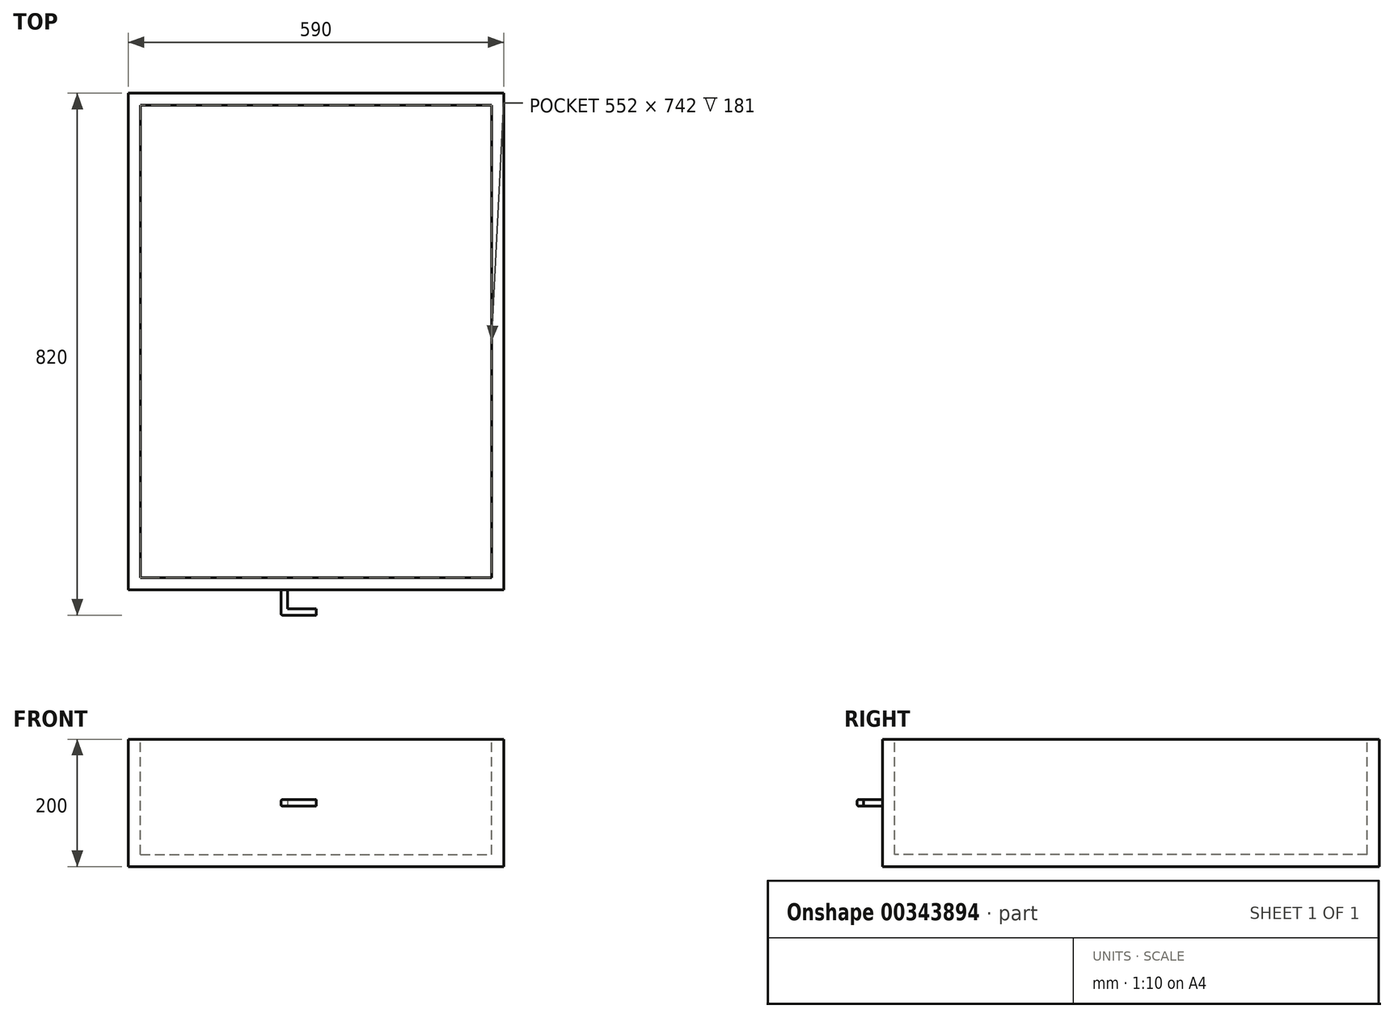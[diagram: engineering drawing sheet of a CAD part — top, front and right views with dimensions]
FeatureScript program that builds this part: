
annotation { "Feature Type Name" : "Feature", "Feature Type Description" : "" }
export const myFeature = defineFeature(function(context is Context, id is Id, definition is map)
    precondition{}
    {
        {
            var Q0;
            Q0=qCreatedBy(makeId("Front.planeOp"),FACE);
            var sketch = newSketch(context, id + "F0", { "sketchPlane" : qUnion([Q0])});
            skLineSegment(sketch, "E0.bottom", {"start": v(-295, 100) * mm, "end": v(295, 100) * mm});
            skLineSegment(sketch, "E0.top", {"start": v(-295, -100) * mm, "end": v(295, -100) * mm});
            skLineSegment(sketch, "E0.left", {"start": v(-295, 100) * mm, "end": v(-295, -100) * mm});
            skLineSegment(sketch, "E0.right", {"start": v(295, 100) * mm, "end": v(295, -100) * mm});
            skPoint(sketch, "E0.middle", {"position": v(0, 0) * mm});
            skSolve(sketch);
        }
        {
            var Q0;
            Q0 = qSketchRegion(id + "F0", true);
            extrude(context, id + "F1", {"entities" : qUnion([Q0]), "depth" : 780 * mm});
        }
        {
            var Q0;
            Q0=makeQuery(id+"F1.opExtrude","SWEPT_FACE",FACE,{"disambiguationData":[OSD([sQuery(id+"F0.wireOp",EDGE,"E0.bottom")])]});
            var sketch = newSketch(context, id + "F2", { "sketchPlane" : qUnion([Q0])});
            skLineSegment(sketch, "E1.bottom", {"start": v(-276, -19) * mm, "end": v(276, -19) * mm});
            skLineSegment(sketch, "E1.top", {"start": v(-276, -761) * mm, "end": v(276, -761) * mm});
            skLineSegment(sketch, "E1.left", {"start": v(-276, -19) * mm, "end": v(-276, -761) * mm});
            skLineSegment(sketch, "E1.right", {"start": v(276, -19) * mm, "end": v(276, -761) * mm});
            skSolve(sketch);
        }
        {
            var Q0;
            Q0=makeQuery(id+"F2.imprint","IMPRINT",FACE,{"disambiguationData":[TD([[makeQuery(id+"F2.imprint","IMPRINT",EDGE,{"derivedFrom":sQuery(id+"F2.wireOp",EDGE,"E1.bottom")}),-1.0]])]});
            extrude(context, id + "F3", {"entities" : qUnion([Q0]), "operationType" : NewBodyOperationType.REMOVE, "oppositeDirection" : true, "depth" : 181 * mm});
        }
        {
            var Q0;
            Q0=makeQuery(id+"F1.opExtrude","CAP_FACE",FACE,{"disambiguationData":[OSD([sQuery(id+"F0.wireOp",EDGE,"E0.bottom"),sQuery(id+"F0.wireOp",EDGE,"E0.top"),sQuery(id+"F0.wireOp",EDGE,"E0.left"),sQuery(id+"F0.wireOp",EDGE,"E0.right")])],"isStart":false});
            var sketch = newSketch(context, id + "F4", { "sketchPlane" : qUnion([Q0])});
            skLineSegment(sketch, "E2.bottom", {"start": v(-45, 5) * mm, "end": v(-55, 5) * mm});
            skLineSegment(sketch, "E2.top", {"start": v(-45, -5) * mm, "end": v(-55, -5) * mm});
            skLineSegment(sketch, "E2.left", {"start": v(-45, 5) * mm, "end": v(-45, -5) * mm});
            skLineSegment(sketch, "E2.right", {"start": v(-55, 5) * mm, "end": v(-55, -5) * mm});
            skPoint(sketch, "E2.middle", {"position": v(-50, 0) * mm});
            skLineSegment(sketch, "E3", {"start": v(-50, 0) * mm, "end": v(0, 0) * mm, "construction": true});
            skSolve(sketch);
        }
        {
            var Q0;
            Q0 = qSketchRegion(id + "F4", true);
            extrude(context, id + "F5", {"entities" : qUnion([Q0]), "operationType" : NewBodyOperationType.ADD, "depth" : 40 * mm});
        }
        {
            var Q0;
            Q0=makeQuery(id+"F5.opExtrude","SWEPT_FACE",FACE,{"disambiguationData":[OSD([sQuery(id+"F4.wireOp",EDGE,"E2.left")])]});
            var sketch = newSketch(context, id + "F6", { "sketchPlane" : qUnion([Q0])});
            skLineSegment(sketch, "E4.bottom", {"start": v(-820, 5) * mm, "end": v(-810, 5) * mm});
            skLineSegment(sketch, "E4.top", {"start": v(-820, -5) * mm, "end": v(-810, -5) * mm});
            skLineSegment(sketch, "E4.left", {"start": v(-820, 5) * mm, "end": v(-820, -5) * mm});
            skLineSegment(sketch, "E4.right", {"start": v(-810, 5) * mm, "end": v(-810, -5) * mm});
            skSolve(sketch);
        }
        {
            var Q0;
            Q0 = qSketchRegion(id + "F6", true);
            var Q1;
            Q1=qCreatedBy(makeId("Right.planeOp"),FACE);
            extrude(context, id + "F7", {"entities" : qUnion([Q0]), "operationType" : NewBodyOperationType.ADD, "endBound" : BoundingType.UP_TO_SURFACE, "endBoundEntityFace" : qUnion([Q1]), "depth" : 25 * mm});
        }
        {
            var Q0;
            {var subQ0=sQuery(id+"F6.wireOp",EDGE,"E4.left");var subQ1=sQuery(id+"F6.wireOp",EDGE,"E4.bottom");var subQ2=sQuery(id+"F4.wireOp",EDGE,"E2.bottom");Q0=makeQuery(id+"FwasGqPcXIY0o4f_1.1.F7.boolean.opBoolean","MERGE",EDGE,{"derivedFrom":[makeQuery(id+"F7.boolean.opBoolean","MERGE",EDGE,{"derivedFrom":[makeQuery(id+"F5.opExtrude","CAP_EDGE",EDGE,{"disambiguationData":[OSD([subQ2])],"isStart":false}),makeQuery(id+"F7.opExtrude","SWEPT_EDGE",EDGE,{"disambiguationData":[OSD([subQ1,subQ0])]})]}),makeQuery(id+"FwasGqPcXIY0o4f_1.1.F5.opExtrude","CAP_EDGE",EDGE,{"disambiguationData":[OSD([subQ2])],"isStart":false}),makeQuery(id+"FwasGqPcXIY0o4f_1.1.F7.opExtrude","SWEPT_EDGE",EDGE,{"disambiguationData":[OSD([subQ1,subQ0])]})]});}
            fillet(context, id + "F8", {"entities" : qUnion([Q0]), "radius" : 2 * mm, "tangentPropagation" : true, "allowEdgeOverflow" : false});
        }
        {
            var Q0;
            {var subQ0=sQuery(id+"F6.wireOp",EDGE,"E4.left");var subQ1=sQuery(id+"F6.wireOp",EDGE,"E4.top");var subQ2=sQuery(id+"F4.wireOp",EDGE,"E2.top");Q0=makeQuery(id+"FwasGqPcXIY0o4f_1.1.F7.boolean.opBoolean","MERGE",EDGE,{"derivedFrom":[makeQuery(id+"F7.boolean.opBoolean","MERGE",EDGE,{"derivedFrom":[makeQuery(id+"F5.opExtrude","CAP_EDGE",EDGE,{"disambiguationData":[OSD([subQ2])],"isStart":false}),makeQuery(id+"F7.opExtrude","SWEPT_EDGE",EDGE,{"disambiguationData":[OSD([subQ1,subQ0])]})]}),makeQuery(id+"FwasGqPcXIY0o4f_1.1.F5.opExtrude","CAP_EDGE",EDGE,{"disambiguationData":[OSD([subQ2])],"isStart":false}),makeQuery(id+"FwasGqPcXIY0o4f_1.1.F7.opExtrude","SWEPT_EDGE",EDGE,{"disambiguationData":[OSD([subQ1,subQ0])]})]});}
            fillet(context, id + "F9", {"entities" : qUnion([Q0]), "radius" : 2 * mm, "tangentPropagation" : true, "allowEdgeOverflow" : false});
        }
        {
            var Q0;
            Q0=makeQuery(id+"F5.opExtrude","SWEPT_EDGE",EDGE,{"disambiguationData":[OSD([sQuery(id+"F4.wireOp",EDGE,"E2.bottom"),sQuery(id+"F4.wireOp",EDGE,"E2.right")])]});
            var Q1;
            Q1=makeQuery(id+"F5.opExtrude","SWEPT_EDGE",EDGE,{"disambiguationData":[OSD([sQuery(id+"F4.wireOp",EDGE,"E2.top"),sQuery(id+"F4.wireOp",EDGE,"E2.right")])]});
            var Q2;
            Q2=makeQuery(id+"FwasGqPcXIY0o4f_1.1.F5.opExtrude","SWEPT_EDGE",EDGE,{"disambiguationData":[OSD([sQuery(id+"F4.wireOp",EDGE,"E2.bottom"),sQuery(id+"F4.wireOp",EDGE,"E2.right")])]});
            var Q3;
            Q3=makeQuery(id+"FwasGqPcXIY0o4f_1.1.F5.opExtrude","SWEPT_EDGE",EDGE,{"disambiguationData":[OSD([sQuery(id+"F4.wireOp",EDGE,"E2.top"),sQuery(id+"F4.wireOp",EDGE,"E2.right")])]});
            fillet(context, id + "F10", {"entities" : qUnion([Q0, Q1, Q2, Q3]), "radius" : 2 * mm, "tangentPropagation" : true, "allowEdgeOverflow" : false});
        }
    });
